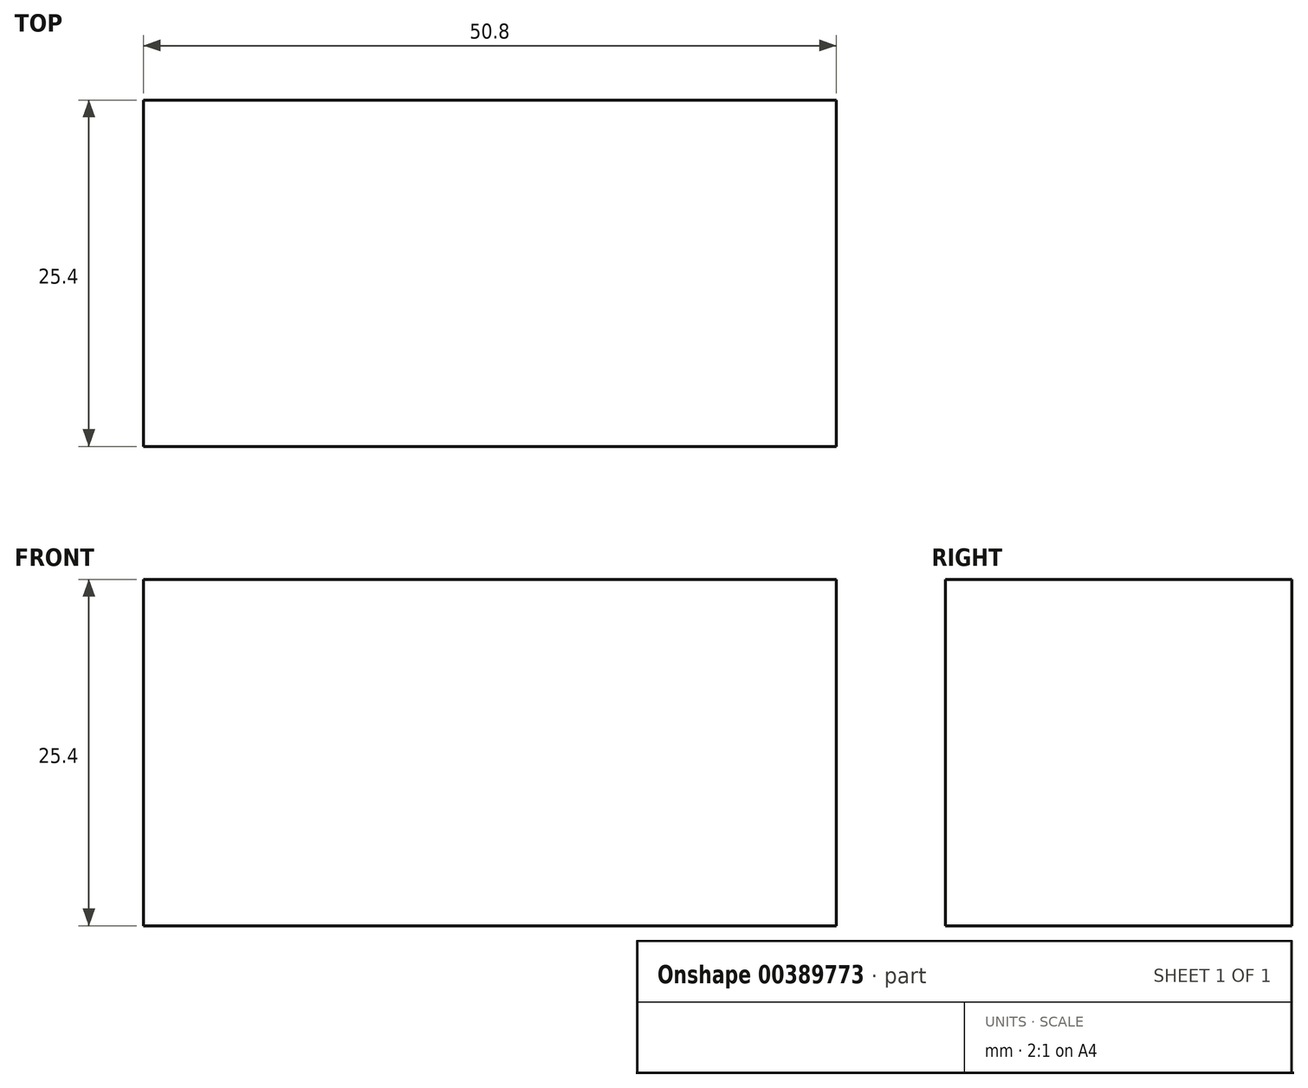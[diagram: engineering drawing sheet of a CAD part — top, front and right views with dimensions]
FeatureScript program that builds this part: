
annotation { "Feature Type Name" : "Feature", "Feature Type Description" : "" }
export const myFeature = defineFeature(function(context is Context, id is Id, definition is map)
    precondition{}
    {
        {
            var Q0;
            Q0=qCreatedBy(makeId("Front.planeOp"),FACE);
            var sketch = newSketch(context, id + "F0", { "sketchPlane" : qUnion([Q0])});
            skLineSegment(sketch, "E0.bottom", {"start": v(0, 0) * mm, "end": v(25.4, 0) * mm});
            skLineSegment(sketch, "E0.top", {"start": v(0, 25.4) * mm, "end": v(25.4, 25.4) * mm});
            skLineSegment(sketch, "E0.left", {"start": v(0, 0) * mm, "end": v(0, 25.4) * mm});
            skLineSegment(sketch, "E0.right", {"start": v(25.4, 0) * mm, "end": v(25.4, 25.4) * mm});
            skLineSegment(sketch, "E1.bottom", {"start": v(0, 0) * mm, "end": v(-25.4, 0) * mm});
            skLineSegment(sketch, "E1.top", {"start": v(0, 25.4) * mm, "end": v(-25.4, 25.4) * mm});
            skLineSegment(sketch, "E1.right", {"start": v(-25.4, 0) * mm, "end": v(-25.4, 25.4) * mm});
            skSolve(sketch);
        }
        {
            var Q0;
            Q0 = qSketchRegion(id + "F0", true);
            extrude(context, id + "F1", {"entities" : qUnion([Q0]), "depth" : 25.4 * mm});
        }
    });
